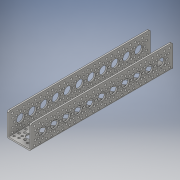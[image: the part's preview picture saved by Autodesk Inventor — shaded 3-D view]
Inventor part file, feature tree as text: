
AUTODESK INVENTOR PART (.ipt)
format: ipt  version: 2016 (Build 200138000, 138)  size: 752,128 bytes
history: native  units: in
note: dims shown in document units (in); Inventor stores cm internally (conversion verified against a paired STEP export)
features: fillet x1
ambient origin geometry x8: Origin, YZ Plane, XZ Plane, XY Plane, X Axis, Y Axis, Z Axis, Center Point
bodies: Solid1 (feature_tree)
feature tree (1):
  fillet  "Fillet1"  [1 undecoded]
note: 1 required parameter value undecoded (feature->parameter linkage not recoverable at this tier; creation-order binding heuristic only, values carry confidence <= 0.55)
